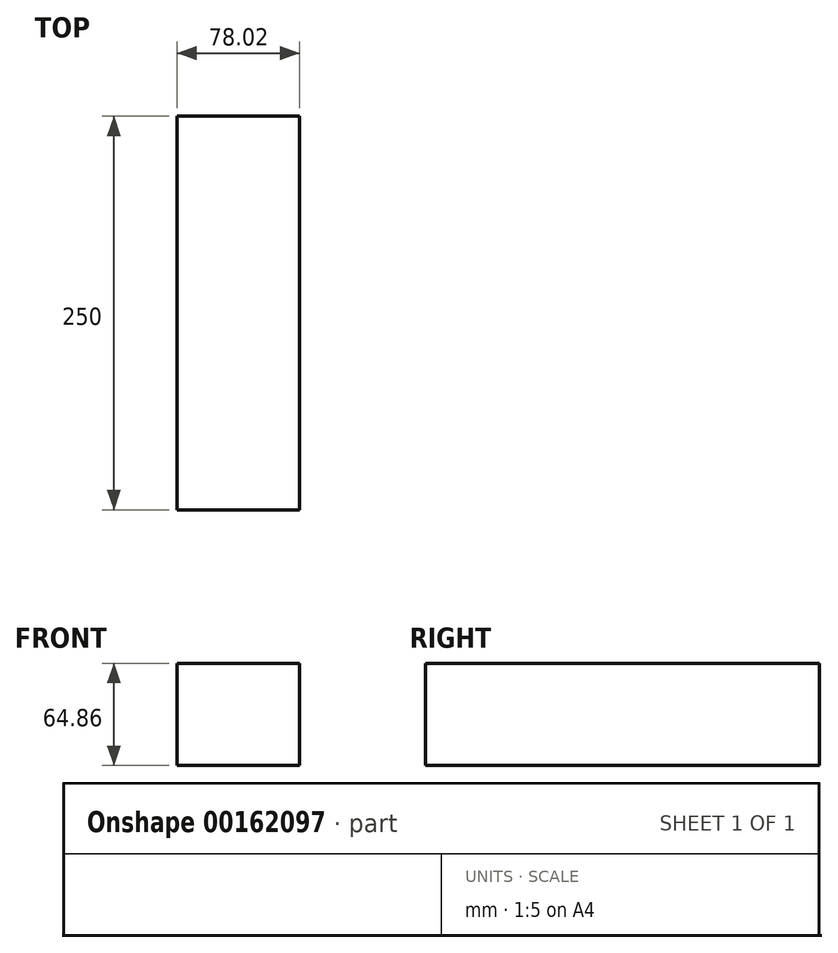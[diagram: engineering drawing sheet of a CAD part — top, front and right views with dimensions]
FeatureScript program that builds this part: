
annotation { "Feature Type Name" : "Feature", "Feature Type Description" : "" }
export const myFeature = defineFeature(function(context is Context, id is Id, definition is map)
    precondition{}
    {
        {
            var Q0;
            Q0=qCreatedBy(makeId("Front.planeOp"), FACE);
            var sketch = newSketch(context, id + "F0", { "sketchPlane" : qUnion([Q0])});
            skLineSegment(sketch, "E0.bottom", {"start": v(0, 0) * mm, "end": v(78.02, 0) * mm});
            skLineSegment(sketch, "E0.top", {"start": v(0, 64.86) * mm, "end": v(78.02, 64.86) * mm});
            skLineSegment(sketch, "E0.left", {"start": v(0, 0) * mm, "end": v(0, 64.86) * mm});
            skLineSegment(sketch, "E0.right", {"start": v(78.02, 0) * mm, "end": v(78.02, 64.86) * mm});
            skSolve(sketch);
        }
        {
            var Q0;
            Q0 = qSketchRegion(id + "F0", true);
            extrude(context, id + "F1", {"entities" : qUnion([Q0]), "depth" : 250 * mm, "offsetDistance" : 25 * mm});
        }
    });
